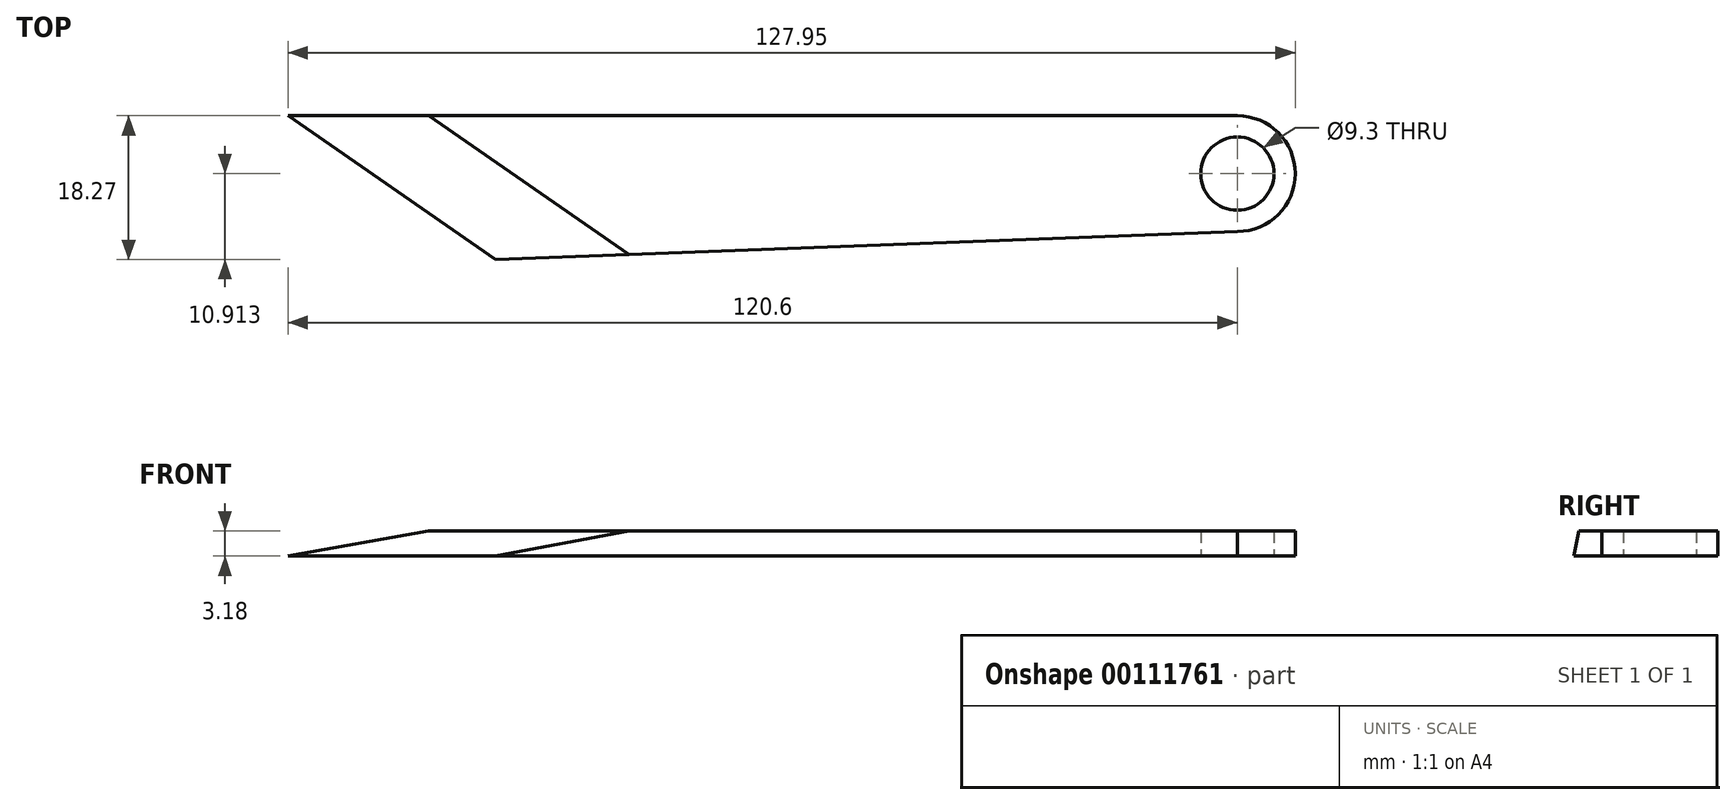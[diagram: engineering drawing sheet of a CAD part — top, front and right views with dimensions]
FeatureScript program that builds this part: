
annotation { "Feature Type Name" : "Feature", "Feature Type Description" : "" }
export const myFeature = defineFeature(function(context is Context, id is Id, definition is map)
    precondition{}
    {
        {
            var Q0;
            Q0=qCreatedBy(makeId("Top.planeOp"),FACE);
            var sketch = newSketch(context, id + "F0", { "sketchPlane" : qUnion([Q0])});
            skLineSegment(sketch, "E0", {"start": v(-65.8, 39.72) * mm, "end": v(54.79, 39.72) * mm});
            skLineSegment(sketch, "E1", {"start": v(-39.43, 21.45) * mm, "end": v(-65.8, 39.72) * mm});
            skLineSegment(sketch, "E2", {"start": v(54.79, 25.01) * mm, "end": v(-39.43, 21.45) * mm});
            skCircle(sketch, "E3", {"center": v(54.79, 32.36) * mm, "radius": 4.65 * mm});
            skArc(sketch, "E4", {"start": v(54.79, 25.01) * mm, "mid": v(62.14, 32.36) * mm, "end": v(54.79, 39.72) * mm});
            skSolve(sketch);
        }
        {
            var Q0;
            Q0=makeQuery(id+"F0.imprint","IMPRINT",FACE,{"disambiguationData":[TD([[makeQuery(id+"F0.imprint","IMPRINT",EDGE,{"derivedFrom":sQuery(id+"F0.wireOp",EDGE,"E0")}),-1.0]])]});
            extrude(context, id + "F1", {"entities" : qUnion([Q0]), "depth" : 3.17 * mm});
        }
        {
            var Q0;
            Q0=makeQuery(id+"F1.opExtrude","CAP_EDGE",EDGE,{"disambiguationData":[OSD([sQuery(id+"F0.wireOp",EDGE,"E1")])],"isStart":false});
            chamfer(context, id + "F2", {"entities" : qUnion([Q0]), "chamferType" : ChamferType.TWO_OFFSETS, "width1" : 3.17 * mm, "oppositeDirection" : false, "width2" : 10.16 * mm, "tangentPropagation" : true});
        }
    });
